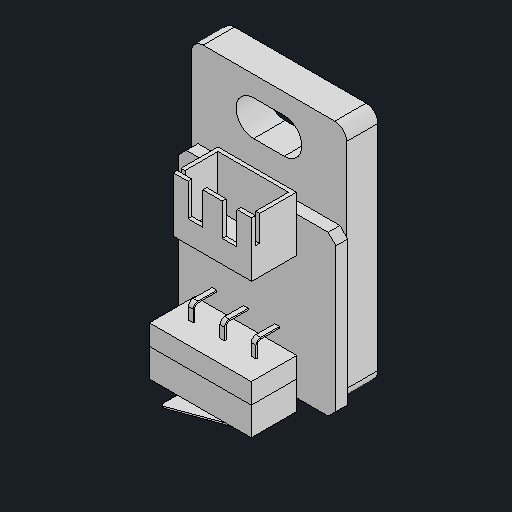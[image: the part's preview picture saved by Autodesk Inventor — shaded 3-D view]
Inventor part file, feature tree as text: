
AUTODESK INVENTOR PART (.ipt)
format: ipt  version: 2024.2 (Build 282272000, 272)  size: 181,760 bytes
history: native  units: mm
features: other x23, extrude x2, chamfer x1
ambient origin geometry x8: Origin, YZ Plane, XZ Plane, XY Plane, X Axis, Y Axis, Z Axis, Center Point
bodies: Body1 (feature_tree), Body2 (feature_tree), Body3 (feature_tree), Body4 (feature_tree), Body5 (feature_tree), Body6 (feature_tree), Body7 (feature_tree), Body8 (feature_tree), Body9 (feature_tree), Body10 (feature_tree), Body11 (feature_tree), Body12 (feature_tree), Body13 (feature_tree)
feature tree (26):
  other  "솔리드1"
  other  "솔리드2"
  other  "솔리드3"
  other  "솔리드4"
  other  "솔리드5"
  other  "솔리드6"
  other  "솔리드7"
  other  "솔리드8"
  other  "솔리드9"
  other  "솔리드10"
  other  "솔리드11"
  other  "솔리드12"
  other  "솔리드13"
  other  "Cut-Extrude1"
  chamfer  "Chamfer1"  [1 undecoded]
  other  "Split1[1]"
  other  "Split1[2]"
  other  "Cut-Extrude3"
  other  "Boss-Extrude5"
  extrude  "Extrude-Thin2"  [1 undecoded]
  other  "LPattern1[1]"
  other  "LPattern1[2]"
  extrude  "Extrude-Thin3"  [1 undecoded]
  other  "LPattern2[1]"
  other  "LPattern2[2]"
  other  "Cut-Extrude4"
note: 3 required parameter values undecoded (feature->parameter linkage not recoverable at this tier; creation-order binding heuristic only, values carry confidence <= 0.55)
